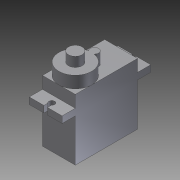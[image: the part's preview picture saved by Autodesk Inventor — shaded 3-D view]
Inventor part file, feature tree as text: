
AUTODESK INVENTOR PART (.ipt)
format: ipt  version: 2011 SP2 (Build 150309200, 309)  size: 145,408 bytes
history: native  units: mm
features: extrude x4, sketch x4, projected_geometry x1
ambient origin geometry x8: Origin, YZ Plane, XZ Plane, XY Plane, X Axis, Y Axis, Z Axis, Center Point
bodies: Solid1 (feature_tree)
feature tree (9):
  extrude  "Extrusion1"  Depth=15.6mm
  extrude  "Extrusion2"  Depth=2.4mm
  extrude  "Extrusion3"  Depth=22.75mm
  extrude  "Extrusion4"  Depth=2.4mm
  sketch  "Sketch1"  dims[d0=11.375mm d1=15.6mm]
  sketch  "Sketch2"  dims[d2=4.825mm d3=2.4mm]
  sketch  "Sketch3"  dims[d4=4.4mm d5=22.75mm]
  sketch  "Sketch4"  dims[d7=4.825mm d8=2.4mm d9=18.0mm d10=12.0mm d11=0.0mm d13=3.0mm d14=4.3mm d15=0.0mm d16=5.0mm d17=3.5mm d18=0.0mm d19=2.1mm d20=2.1mm d21=27.9mm d22=2.25mm d23=1.3mm d25=0.65mm d26=1.3mm d27=0.65mm d28=3.5mm d29=0.0mm]
  projected_geometry  "Projected Loop1"
